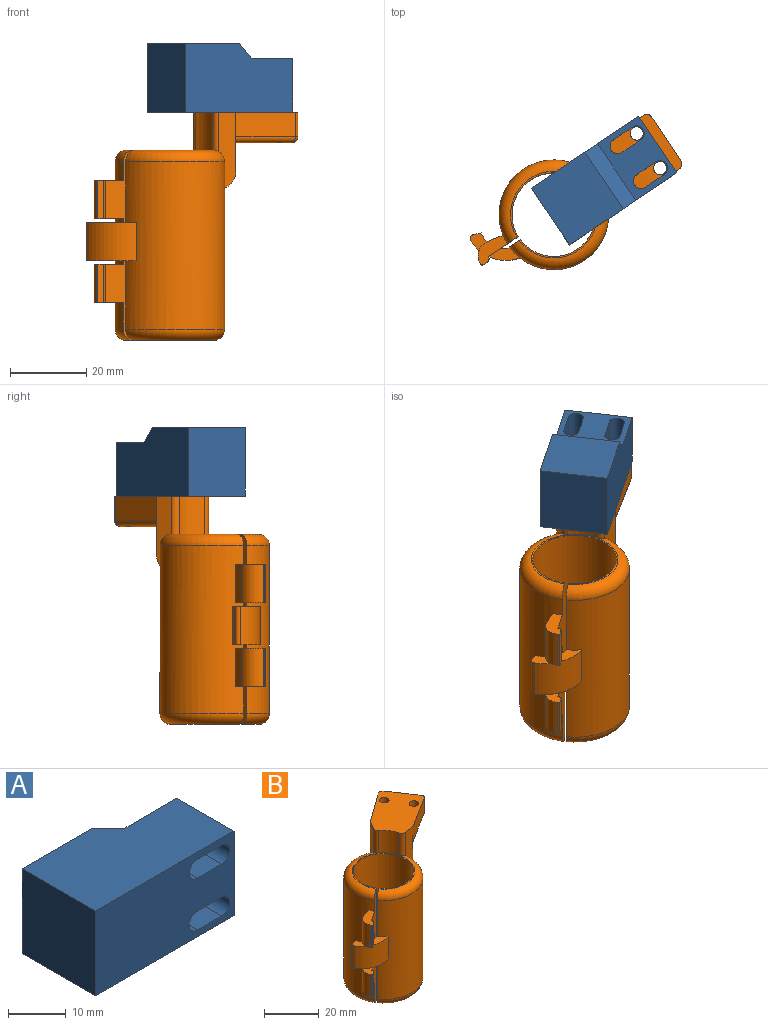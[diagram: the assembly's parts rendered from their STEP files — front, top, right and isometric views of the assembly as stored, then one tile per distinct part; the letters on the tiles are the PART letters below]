
ASSEMBLY  parts=2 mates=1
PART A: 16 faces, bbox 34x18x18 mm
  f0: plane 34x18mm, normal (0,-1,0), area 538.9mm2, adj f2,f5,f6,f7,f8,f9,f10,f11
  f1: plane 18x13mm, normal (0,1,0), area 160.9mm2, adj f2,f3,f6,f7,f8,f9,f10,f11
  f2: plane 18x14mm, normal (1,0,0), area 252mm2, adj f0,f1,f6,f7
  f3: plane 18x4mm, normal (0.71,0.71,0), area 101.8mm2, adj f1,f4,f6,f7
  f4: plane 18x17mm, normal (0,1,0), area 306mm2, adj f3,f5,f6,f7
  f5: plane 18x18mm, normal (-1,0,0), area 324mm2, adj f0,f4,f6,f7
  f6: plane 34x18mm, normal (0,0,1), area 552mm2, adj f0,f1,f2,f3,f4,f5
  f7: plane 34x18mm, normal (0,0,-1), area 552mm2, adj f0,f1,f2,f3,f4,f5
  f8: plane 14x6mm, normal (0,0,1), area 84mm2, adj f0,f1,f9,f11
  f9: cylinder r=2mm len=14mm, axis (0,-1,0), area 88mm2, adj f0,f1,f8,f10
  f10: plane 14x6mm, normal (0,0,-1), area 84mm2, adj f0,f1,f9,f11
  f11: cylinder r=2mm len=14mm, axis (0,-1,0), area 88mm2, adj f0,f1,f8,f10
  f12: cylinder r=2mm len=14mm, axis (0,-1,0), area 88mm2, adj f0,f1,f13,f15
  f13: plane 14x6mm, normal (0,0,-1), area 84mm2, adj f0,f1,f12,f14
  f14: cylinder r=2mm len=14mm, axis (0,-1,0), area 88mm2, adj f0,f1,f13,f15
  f15: plane 14x6mm, normal (0,0,1), area 84mm2, adj f0,f1,f12,f14
PART B: 51 faces, bbox 55.7x42x60.1 mm
  f0: cylinder r=11mm len=49mm, axis (0,0,-1), area 3337.6mm2, adj f3,f4,f37,f39
  f1: plane 27.57x24.75mm, normal (0,0,1), area 368.2mm2, adj f5,f6,f8,f9,f10,f11,f12,f38
  f2: cylinder r=14.4mm len=44.06mm, axis (0,0,-1), area 3757.8mm2, adj f3,f4,f5,f6,f16,f17,f18,f19
  f3: plane 50.02x3.25mm, normal (-0.56,0.83,0), area 171.2mm2, adj f0,f2,f14,f17,f18,f37,f39,f40
  f4: plane 50.02x7.84mm, normal (0.56,-0.83,0), area 286.8mm2, adj f0,f2,f23,f24,f29,f30,f31,f32
  f5: plane 20x4.55mm, normal (0.13,-0.99,0), area 74.6mm2, adj f1,f2,f7,f8,f34,f40,f42
  f6: plane 20x4mm, normal (-0.87,0.49,0), area 74.6mm2, adj f1,f2,f7,f12,f34,f40,f43
  f7: cylinder r=17.5mm len=13.06mm, axis (0,0,1), area 121.6mm2, adj f5,f6,f13,f34,f45,f48
  f8: plane 15.62x9.81mm, normal (0.53,-0.85,0), area 119.9mm2, adj f1,f5,f48,f50
  f9: plane 11.57x7.8mm, normal (0.83,0.56,0), area 90.7mm2, adj f1,f44,f47,f50
  f10: cylinder r=1.75mm len=8mm, axis (0,0,1), area 87.9mm2, adj f1,f13,f45
  f11: cylinder r=1.75mm len=8mm, axis (0,0,1), area 87.9mm2, adj f1,f13,f48
  f12: plane 14.95x10.81mm, normal (-0.59,0.81,0), area 119.9mm2, adj f1,f6,f44,f45
  f13: plane 22.26x21.06mm, normal (0,0,-1), area 210.1mm2, adj f7,f10,f11,f45,f47,f48
  f14: cylinder r=6.44mm len=10mm, axis (0,0,1), area 87.7mm2, adj f3,f15,f17,f18
  f15: plane 10x2.15mm, normal (-0.24,0.97,0), area 22.2mm2, adj f14,f17,f18,f33
  f16: cylinder r=10.83mm len=13.03mm, axis (0,0,1), area 149.7mm2, adj f2,f17,f18,f33
  f17: plane 13.18x7.25mm, normal (0,0,-1), area 40.3mm2, adj f2,f3,f14,f15,f16,f33
  f18: plane 13.18x7.25mm, normal (0,0,1), area 40.3mm2, adj f2,f3,f14,f15,f16,f33
  f19: plane 10x4.07mm, normal (-0.37,0.93,0), area 43.8mm2, adj f2,f23,f24,f36
  f20: cylinder r=11.04mm len=10mm, axis (0,0,1), area 1mm2, adj f21,f23,f24,f36
  f21: cylinder r=23.21mm len=10mm, axis (0,0,1), area 5mm2, adj f20,f22,f23,f24
  f22: plane 10x1.48mm, normal (0.56,-0.83,0), area 17.8mm2, adj f21,f23,f24,f32
  f23: plane 7.99x7.71mm, normal (0,0,-1), area 28.2mm2, adj f2,f4,f19,f20,f21,f22,f32,f36
  f24: plane 7.99x7.71mm, normal (0,0,1), area 28.2mm2, adj f2,f4,f19,f20,f21,f22,f32,f36
  f25: cylinder r=11.04mm len=10mm, axis (0,0,1), area 1mm2, adj f26,f29,f30,f35
  f26: cylinder r=23.21mm len=10mm, axis (0,0,1), area 5mm2, adj f25,f27,f29,f30
  f27: plane 10x1.48mm, normal (0.56,-0.83,0), area 17.8mm2, adj f26,f29,f30,f31
  f28: plane 10x4.07mm, normal (-0.37,0.93,0), area 43.8mm2, adj f2,f29,f30,f35
  f29: plane 7.99x7.71mm, normal (0,0,-1), area 28.2mm2, adj f2,f4,f25,f26,f27,f28,f31,f35
  f30: plane 7.99x7.71mm, normal (0,0,1), area 28.2mm2, adj f2,f4,f25,f26,f27,f28,f31,f35
  f31: cylinder r=1mm len=10mm, axis (0,0,1), area 15.7mm2, adj f4,f27,f29,f30
  f32: cylinder r=1mm len=10mm, axis (0,0,1), area 15.7mm2, adj f4,f22,f23,f24
  f33: cylinder r=1mm len=10mm, axis (0,0,1), area 18.7mm2, adj f15,f16,f17,f18
  f34: torus R=12.5mm, axis (0,0,-1), area 90.5mm2, adj f2,f5,f6,f7
  f35: cylinder r=4mm len=10mm, axis (0,0,1), area 70.2mm2, adj f25,f28,f29,f30
  f36: cylinder r=4mm len=10mm, axis (0,0,1), area 70.2mm2, adj f19,f20,f23,f24
  f37: torus R=12mm, axis (0,0,1), area 110.6mm2, adj f0,f3,f4,f41
  f38: cylinder r=11.5mm len=10mm, axis (0,0,1), area 80.8mm2, adj f1,f40,f42,f43
  f39: plane 22.8x22.8mm, normal (0,0,1), area 27.7mm2, adj f0,f3,f4,f40
  f40: torus R=11.4mm, axis (0,0,1), area 332.7mm2, adj f2,f3,f4,f5,f6,f38,f39,f42
  f41: torus R=11.4mm, axis (0,0,-1), area 345.6mm2, adj f2,f3,f4,f37
  f42: cylinder r=1.5mm len=10.41mm, axis (0,0,1), area 22mm2, adj f1,f5,f38,f40
  f43: cylinder r=1.5mm len=10.41mm, axis (0,0,1), area 22mm2, adj f1,f6,f38,f40
  f44: cylinder r=1.5mm len=6.5mm, axis (0,0,-1), area 15.6mm2, adj f1,f9,f12,f46
  f45: cylinder r=1.5mm len=15.83mm, axis (0.81,0.59,0), area 42.3mm2, adj f7,f10,f12,f13,f46
  f46: sphere r=1.5mm, area 3.6mm2, adj f44,f45,f47
  f47: cylinder r=1.5mm len=12.41mm, axis (0.56,-0.83,0), area 32.9mm2, adj f9,f13,f46,f49
  f48: cylinder r=1.5mm len=16.42mm, axis (-0.85,-0.53,0), area 42.3mm2, adj f7,f8,f11,f13,f49
  f49: sphere r=1.5mm, area 3.6mm2, adj f47,f48,f50
  f50: cylinder r=1.5mm len=6.5mm, axis (0,0,1), area 15.6mm2, adj f1,f8,f9,f49
PLACE A rot(axis=(0.92,0.28,0.28),94.9deg) t=(-3.53,25.66,60.27)mm
PLACE B t=(-11.25,-3.11,0.22)mm fixed
MATE parallel A.f0 <-> B.f1  axis (0,0,-1) through (14.36,26.85,60.27)mm
